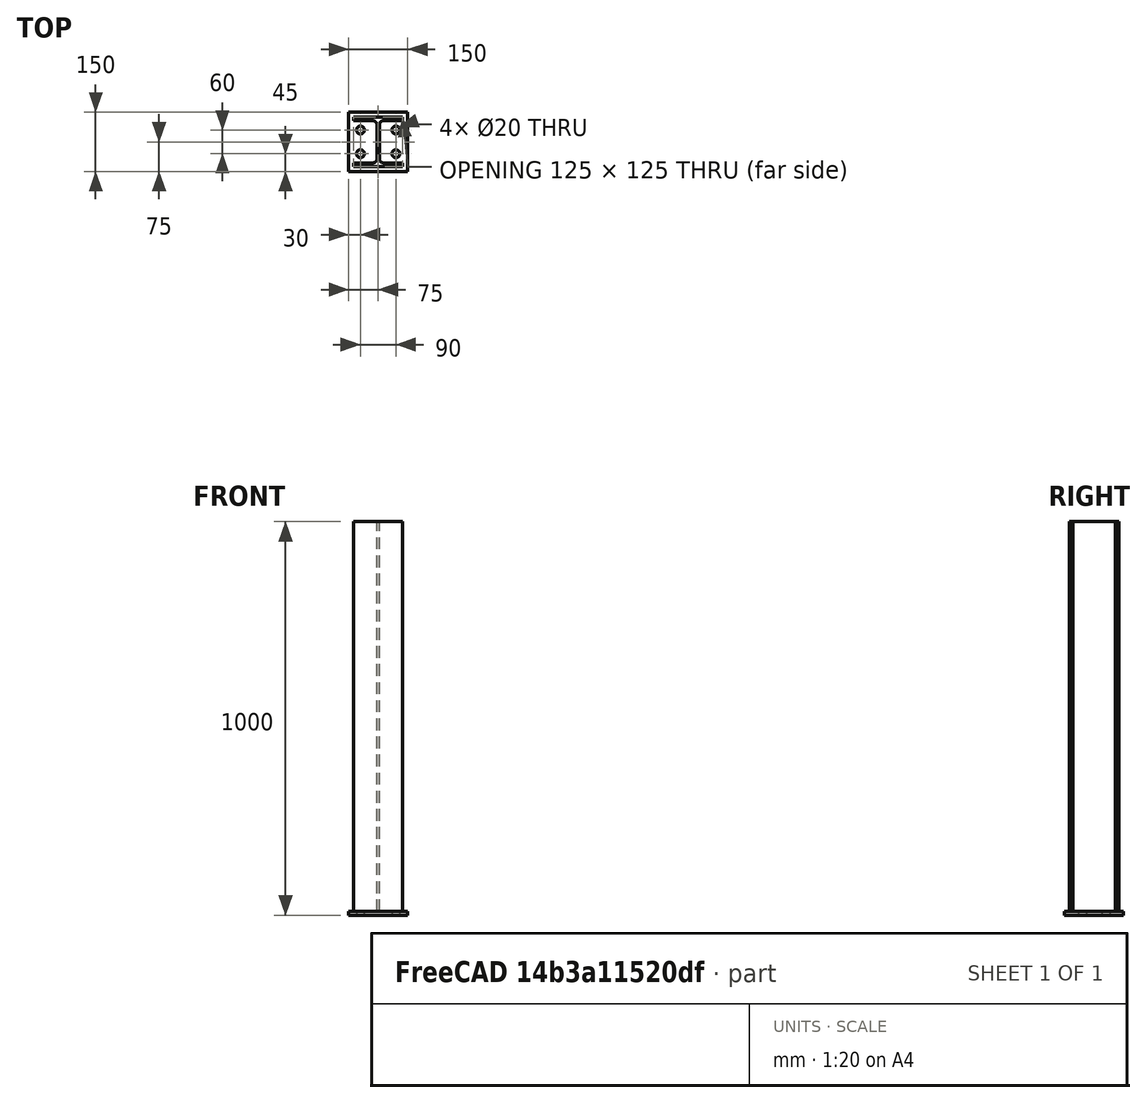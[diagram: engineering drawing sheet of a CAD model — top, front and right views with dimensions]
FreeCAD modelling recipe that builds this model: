
FCSTD DOCUMENT  (FreeCAD 0.21R30492 (Git))
Label: 03_Pst_H
License: All rights reserved
LicenseURL: http://en.wikipedia.org/wiki/All_rights_reserved
objects: Part::FeaturePython×2, Part::Extrusion×1, Part::MultiFuse×1
note: 4 computed .brp shape members not serialized (recipe doc carries the construction recipe); baked Part::Feature solids carry a one-line shape summary decoded from their .brp

FEATURE [Part::FeaturePython] BasePlate  # WARN: FeaturePython — macro-defined, semantics opaque (R4)
  B = 150
  D = 20
  H = 150
  b1 = 30
  h1 = 45
  sface = 0
FEATURE [Part::Extrusion] Extrude
  Base = -> BasePlate
  Dir = (0,0,1)
  DirMode = 2
  FaceMakerClass = Part::FaceMakerBullseye
  LengthFwd = 10
  LengthRev = 0
  Solid = true
  Symmetric = false
FEATURE [Part::FeaturePython] H_Shape  # WARN: FeaturePython — macro-defined, semantics opaque (R4)
  B = 125
  H = 125
  L = 1000
  Solid = true
  g0 = 7.85
  mass = 23.796
  size = 1
  standard = SS_Wide
FEATURE [Part::MultiFuse] Fusion  label="PostH"
  Shapes = -> [Extrude,H_Shape]
